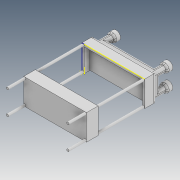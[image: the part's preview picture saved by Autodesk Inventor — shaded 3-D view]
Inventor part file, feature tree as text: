
AUTODESK INVENTOR PART (.ipt)
format: ipt  version: 2021 (Build 250183000, 183)  size: 536,576 bytes
history: native  units: in
note: dims shown in document units (in); Inventor stores cm internally (conversion verified against a paired STEP export)
features: sketch x10, extrude x7, fillet x3, other x1
ambient origin geometry x8: Origin, YZ Plane, XZ Plane, XY Plane, X Axis, Y Axis, Z Axis, Center Point
bodies: Body1 (feature_tree), Body2 (feature_tree)
feature tree (21):
  other  "Sólido1"
  extrude  "Extrusão1"  Depth=0.7874in
  extrude  "Extrusão2"  Depth=0.1969in
  extrude  "Extrusão3"  Depth=0.3937in TaperAngle=0.0deg
  sketch  "Esboço4"  dims[d8=0.0787in d9=0.8661in]
  extrude  "Extrusão4"  Depth=0.8661in
  sketch  "Esboço7"  dims[d13=0.0787in d14=0.0787in d15=0.0787in d16=0.0787in]
  sketch  "Esboço8"  dims[d17=0.0787in d18=1.5748in d19=0.0in d29=0.3937in]
  extrude  "Extrusão5"  Depth=0.3937in TaperAngle=0.0deg
  extrude  "Extrusão6"  Depth=0.0787in
  fillet  "Arredondamento1"  Radius=0.0787in
  fillet  "Arredondamento2"  Radius=0.0787in
  extrude  "Extrusão7"  Depth=1.5748in TaperAngle=0.0deg
  fillet  "Arredondamento3"  Radius=0.3937in
  sketch  "Esboço1"  dims[d0=1.9685in d1=0.7874in]
  sketch  "Esboço2"  dims[d2=0.3937in d3=0.0in d4=0.1969in]
  sketch  "Esboço3"  dims[d5=0.1969in d6=0.3937in d7=0.0in]
  sketch  "Esboço5"  dims[d10=2.126in d11=0.3937in d12=0.0in]
  sketch  "Esboço9"  dims[d30=0.8661in d31=0.0in]
  sketch  "Esboço10"  dims[d32=0.0787in]
  sketch  "Esboço11"  dims[d33=0.5906in d34=0.0in d35=0.0787in d36=0.0787in d37=0.2953in d38=0.2953in d39=1.063in d40=0.1969in d41=0.0in d42=0.0787in d43=0.0344in]
